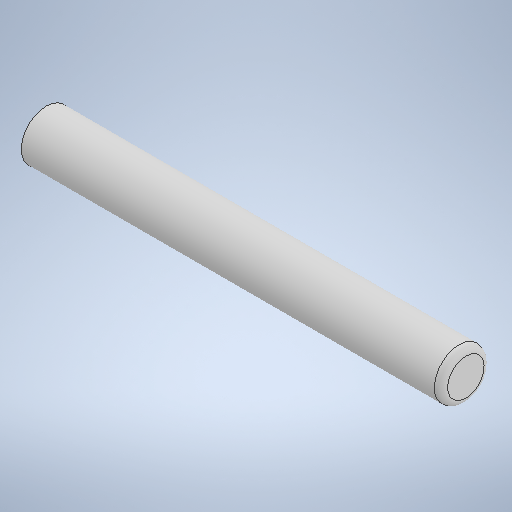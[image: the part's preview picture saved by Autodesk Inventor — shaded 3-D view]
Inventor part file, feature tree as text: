
AUTODESK INVENTOR PART (.ipt)
format: ipt  version: 2025 (Build 290162000, 162)  size: 245,760 bytes
history: native  units: in
note: dims shown in document units (in); Inventor stores cm internally (conversion verified against a paired STEP export)
features: sketch x2, revolve x1, extrude x1
ambient origin geometry x8: Origin, YZ Plane, XZ Plane, XY Plane, X Axis, Y Axis, Z Axis, Center Point
bodies: Solid1 (feature_tree)
feature tree (4):
  revolve  "Revolution1"  [1 undecoded]
  extrude  "Extrusion2"  Depth=0.0787in
  sketch  "Sketch1"  dims[d0=3.937in d2=0.2953in]
  sketch  "Sketch3"  dims[d3=90.0deg d8=0.0787in d9=0.3205in d10=0.126in d11=0.0in]
note: 1 required parameter value undecoded (feature->parameter linkage not recoverable at this tier; creation-order binding heuristic only, values carry confidence <= 0.55)
